# Revit family: 3-677-xx - 37-677-xx - Ellipse (Pendant)
name_source: partatom
category: Lighting Fixtures
revit_build: Autodesk Revit 2017 (Build: 20160225_1515(x64)
units: mm (PartAtom-declared; Revit-internal decimal feet)

## family parameters
Always vertical = Yes
Cut with Voids When Loaded = No
Host = Ceiling
Light Source = Yes
OmniClass Number = 23.80.70.11
OmniClass Title = Luminaries for Internal Lighting
Part Type = Normal
Room Calculation Point = No
Round Connector Dimension = Use Diameter
Shared = No

## types (6) — shared parameters
2nd Diffuser = <By Category>
Color Filter = 16777215
Dimming Lamp Color Temperature Shift = <None>
Emit Shape Visible in Rendering = No
Emit from Circle Diameter = 24 "
Lamp = LED Array
Manufacturer = Oxygen Lighting & Fans
Model = 3-677-XX / 37-677-XX - Ellipse
Other 1 = Braided Cord
Other 2 = <By Category>
Supplied with = Supplied with 8 ft of braided cord
Tilt Angle = 0.00°
URL = www.oxygenlighting.com
Wattage Comments = 7.11 W at 120 V

## per-type parameters (varying)
| type | Main Diffuser | Metal Finish | Photometric Web File |
| 3-677-115 / 37-677-115 - Ellipse | White Opal Glass | 15 - Black | 3-677-124 Ellipse Pendant with Glass Enclosure.ies |
| 3-677-120 / 37-677-120 - Ellipse | White Opal Glass | 20 - Polished Nickel | 3-677-124 Ellipse Pendant with Glass Enclosure.ies |
| 3-677-124 / 37-677-124 - Ellipse | White Opal Glass | 24 - Satin Nickel | 3-677-124 Ellipse Pendant with Glass Enclosure.ies |
| 3-677-215 / 37-677-215 - Ellipse | Matte White Acrylic | 15 - Black | 3-677-215 Ellipse Pendant with Acrylic Enclosure.ies |
| 3-677-220 / 37-677-220 - Ellipse | Matte White Acrylic | 20 - Polished Nickel | 3-677-215 Ellipse Pendant with Acrylic Enclosure.ies |
| 3-677-224 / 37-677-224 - Ellipse | Matte White Acrylic | 24 - Satin Nickel | 3-677-215 Ellipse Pendant with Acrylic Enclosure.ies |

## geometry (parser evidence)
native form markers: Sweep x6
no freeform markers — native parametric forms only
